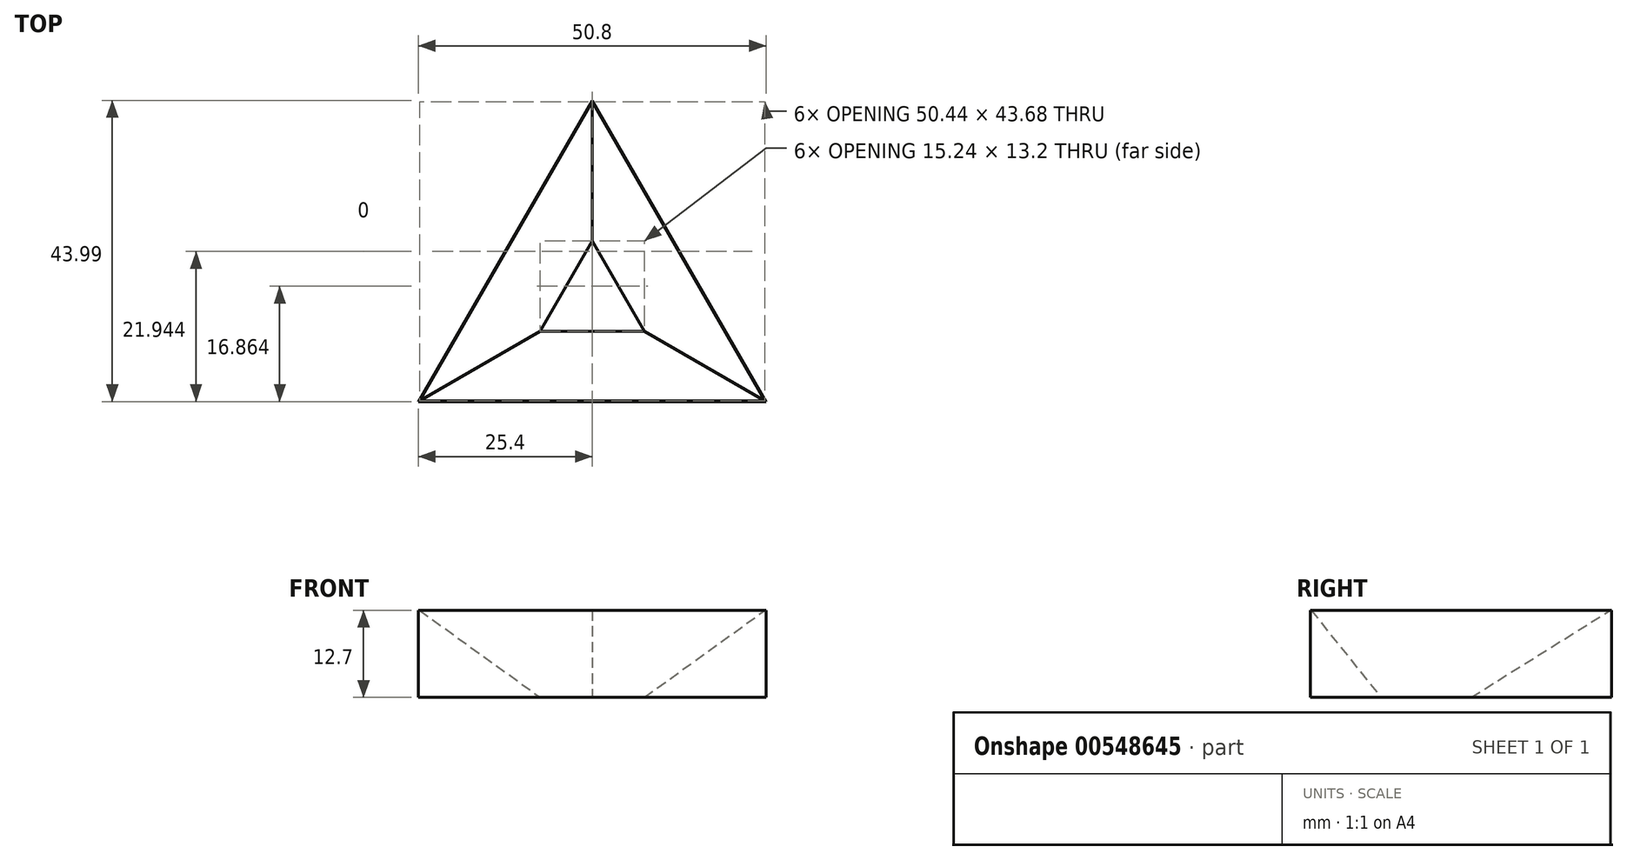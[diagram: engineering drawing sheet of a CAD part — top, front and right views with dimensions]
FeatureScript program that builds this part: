
annotation { "Feature Type Name" : "Feature", "Feature Type Description" : "" }
export const myFeature = defineFeature(function(context is Context, id is Id, definition is map)
    precondition{}
    {
        {
            var Q0;
            Q0=qCreatedBy(makeId("Top.planeOp"),FACE);
            var sketch = newSketch(context, id + "F0", { "sketchPlane" : qUnion([Q0])});
            skLineSegment(sketch, "E0", {"start": v(-25.4, 0) * mm, "end": v(25.4, 0) * mm});
            skLineSegment(sketch, "E1", {"start": v(-25.4, 0) * mm, "end": v(0, 44) * mm});
            skLineSegment(sketch, "E2", {"start": v(0, 44) * mm, "end": v(25.4, 0) * mm});
            skLineSegment(sketch, "E3", {"start": v(-7.62, 10.27) * mm, "end": v(7.62, 10.27) * mm});
            skLineSegment(sketch, "E4", {"start": v(-7.62, 10.27) * mm, "end": v(0, 23.46) * mm});
            skLineSegment(sketch, "E5", {"start": v(0, 23.46) * mm, "end": v(7.62, 10.27) * mm});
            skPoint(sketch, "E6", {"position": v(0, 10.27) * mm});
            skLineSegment(sketch, "E7", {"start": v(0, 10.27) * mm, "end": v(0, 0) * mm, "construction": true});
            skLineSegment(sketch, "E8", {"start": v(-7.62, 10.27) * mm, "end": v(-25.4, 0) * mm});
            skLineSegment(sketch, "E9", {"start": v(0, 23.46) * mm, "end": v(0, 44) * mm});
            skLineSegment(sketch, "E10", {"start": v(7.62, 10.27) * mm, "end": v(25.4, 0) * mm});
            skSolve(sketch);
        }
        {
            var Q0;
            Q0=makeQuery(id+"F0.imprint","IMPRINT",FACE,{"disambiguationData":[TD([[makeQuery(id+"F0.imprint","IMPRINT",EDGE,{"derivedFrom":sQuery(id+"F0.wireOp",EDGE,"E1")}),-1.0]])]});
            var Q1;
            Q1=makeQuery(id+"F0.imprint","IMPRINT",FACE,{"disambiguationData":[TD([[makeQuery(id+"F0.imprint","IMPRINT",EDGE,{"derivedFrom":sQuery(id+"F0.wireOp",EDGE,"E2")}),-1.0]])]});
            var Q2;
            Q2=makeQuery(id+"F0.imprint","IMPRINT",FACE,{"disambiguationData":[TD([[makeQuery(id+"F0.imprint","IMPRINT",EDGE,{"derivedFrom":sQuery(id+"F0.wireOp",EDGE,"E0")}),1.0]])]});
            extrude(context, id + "F1", {"entities" : qUnion([Q0, Q1, Q2]), "depth" : 12.7 * mm, "offsetDistance" : 25.4 * mm});
        }
        {
            var Q0;
            Q0=makeQuery(id+"F1.opExtrude","CAP_EDGE",EDGE,{"disambiguationData":[OSD([sQuery(id+"F0.wireOp",EDGE,"E3")])],"isStart":false});
            var Q1;
            Q1=makeQuery(id+"F1.opExtrude","CAP_EDGE",EDGE,{"disambiguationData":[OSD([sQuery(id+"F0.wireOp",EDGE,"E4")])],"isStart":false});
            var Q2;
            Q2=makeQuery(id+"F1.opExtrude","CAP_EDGE",EDGE,{"disambiguationData":[OSD([sQuery(id+"F0.wireOp",EDGE,"E5")])],"isStart":false});
            chamfer(context, id + "F2", {"entities" : qUnion([Q0, Q1, Q2]), "chamferType" : ChamferType.TWO_OFFSETS, "width1" : 12.7 * mm, "oppositeDirection" : false, "width2" : 10.16 * mm, "tangentPropagation" : true});
        }
    });
